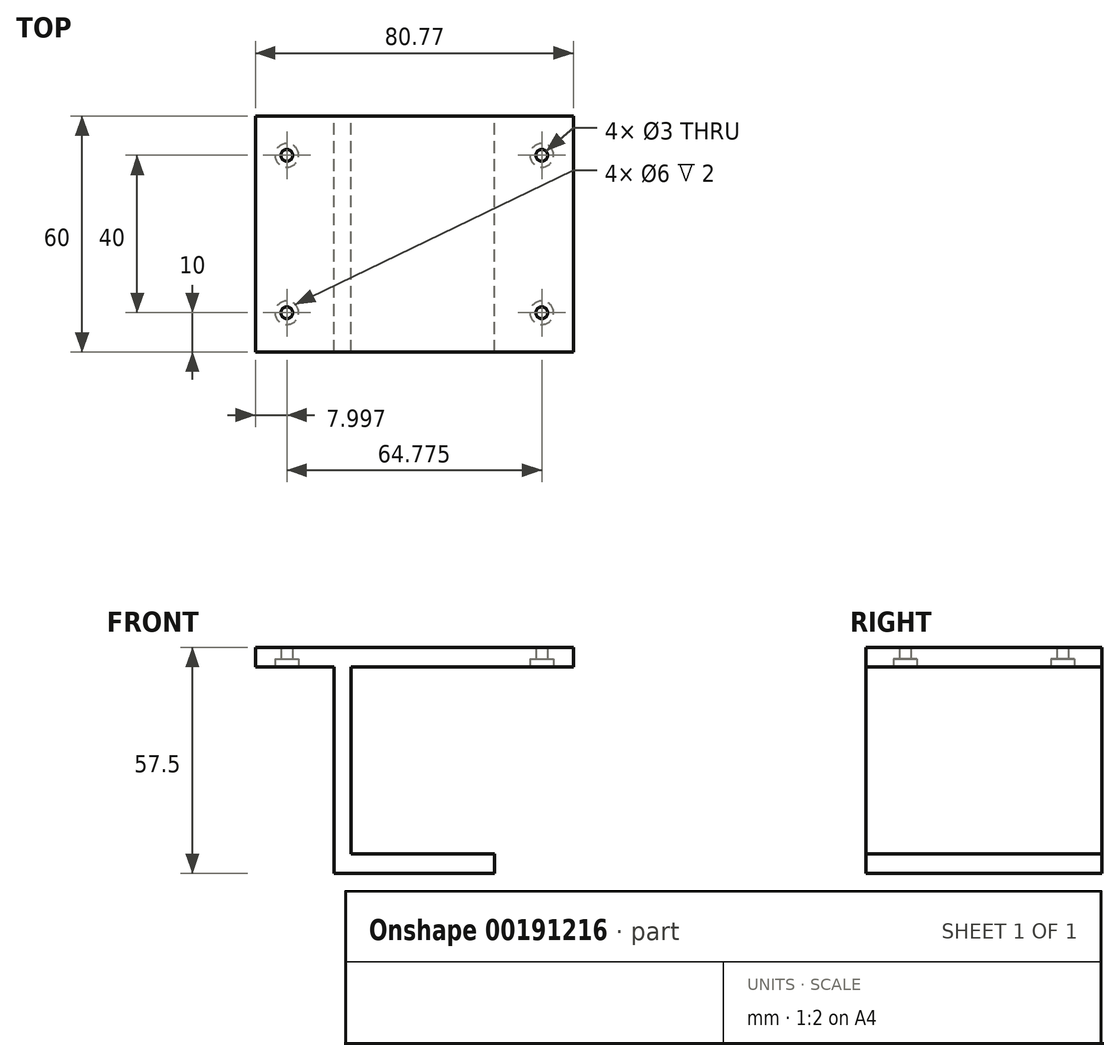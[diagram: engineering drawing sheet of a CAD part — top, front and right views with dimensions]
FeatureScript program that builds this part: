
annotation { "Feature Type Name" : "Feature", "Feature Type Description" : "" }
export const myFeature = defineFeature(function(context is Context, id is Id, definition is map)
    precondition{}
    {
        {
            var Q0;
            Q0=qCreatedBy(makeId("Front.planeOp"),FACE);
            var sketch = newSketch(context, id + "F0", { "sketchPlane" : qUnion([Q0])});
            skLineSegment(sketch, "E0.top", {"start": v(-27.45, -17.57) * mm, "end": v(13.32, -17.57) * mm});
            skLineSegment(sketch, "E0.left", {"start": v(-27.45, 34.93) * mm, "end": v(-27.45, -12.57) * mm});
            skLineSegment(sketch, "E1", {"start": v(13.32, -12.57) * mm, "end": v(-23.18, -12.57) * mm});
            skLineSegment(sketch, "E2", {"start": v(-23.18, -12.57) * mm, "end": v(-23.18, 34.93) * mm});
            skLineSegment(sketch, "E3", {"start": v(-23.18, 34.93) * mm, "end": v(13.32, 34.93) * mm});
            skLineSegment(sketch, "E4", {"start": v(13.32, 39.93) * mm, "end": v(-27.45, 39.93) * mm});
            skPoint(sketch, "E5.orphan", {"position": v(-27.45, 42.43) * mm});
            skLineSegment(sketch, "E6", {"start": v(13.32, 39.93) * mm, "end": v(33.32, 39.93) * mm});
            skLineSegment(sketch, "E7", {"start": v(33.32, 39.93) * mm, "end": v(33.32, 34.93) * mm});
            skLineSegment(sketch, "E8", {"start": v(33.32, 34.93) * mm, "end": v(13.32, 34.93) * mm});
            skLineSegment(sketch, "E9", {"start": v(13.32, -12.57) * mm, "end": v(13.32, -17.57) * mm});
            skLineSegment(sketch, "E10", {"start": v(-27.45, -12.57) * mm, "end": v(-27.45, -17.57) * mm});
            skPoint(sketch, "E11.end.orphan", {"position": v(-49.27, 34.93) * mm});
            skPoint(sketch, "E12.end.orphan", {"position": v(-49.27, -12.57) * mm});
            skLineSegment(sketch, "E13", {"start": v(-27.45, 39.93) * mm, "end": v(-47.45, 39.93) * mm});
            skLineSegment(sketch, "E14", {"start": v(-47.45, 39.93) * mm, "end": v(-47.45, 34.93) * mm});
            skLineSegment(sketch, "E15", {"start": v(-47.45, 34.93) * mm, "end": v(-27.45, 34.93) * mm});
            skSolve(sketch);
        }
        {
            var Q0;
            Q0=makeQuery(id+"F0.imprint","IMPRINT",FACE,{"disambiguationData":[TD([[makeQuery(id+"F0.imprint","IMPRINT",EDGE,{"derivedFrom":sQuery(id+"F0.wireOp",EDGE,"E0.top")}),1.0]])]});
            extrude(context, id + "F1", {"entities" : qUnion([Q0]), "depth" : 60 * mm});
        }
        {
            var Q0;
            Q0=makeQuery(id+"F1.opExtrude","SWEPT_FACE",FACE,{"disambiguationData":[OSD([sQuery(id+"F0.wireOp",EDGE,"E3"),sQuery(id+"F0.wireOp",EDGE,"E8")])]});
            var sketch = newSketch(context, id + "F2", { "sketchPlane" : qUnion([Q0])});
            skPoint(sketch, "E16", {"position": v(-39.45, 50) * mm});
            skPoint(sketch, "E17", {"position": v(-39.45, 10) * mm});
            skPoint(sketch, "E18", {"position": v(25.32, 50) * mm});
            skPoint(sketch, "E19", {"position": v(25.32, 10) * mm});
            skSolve(sketch);
        }
        {
            var Q0;
            Q0=sQuery(id+"F2.wireOp",VERTEX,"E18");
            var Q1;
            Q1=sQuery(id+"F2.wireOp",VERTEX,"E19");
            var Q2;
            Q2=sQuery(id+"F2.wireOp",VERTEX,"E17");
            var Q3;
            Q3=sQuery(id+"F2.wireOp",VERTEX,"E16");
            var Q4;
            Q4=makeQuery(id+"F1.opExtrude","SWEPT_BODY",BODY,{"disambiguationData":[OSD([sQuery(id+"F0.wireOp",EDGE,"E0.top"),sQuery(id+"F0.wireOp",EDGE,"E0.left"),sQuery(id+"F0.wireOp",EDGE,"E1"),sQuery(id+"F0.wireOp",EDGE,"E2"),sQuery(id+"F0.wireOp",EDGE,"E3"),sQuery(id+"F0.wireOp",EDGE,"E4"),sQuery(id+"F0.wireOp",EDGE,"E6"),sQuery(id+"F0.wireOp",EDGE,"E7"),sQuery(id+"F0.wireOp",EDGE,"E8"),sQuery(id+"F0.wireOp",EDGE,"E9"),sQuery(id+"F0.wireOp",EDGE,"E10"),sQuery(id+"F0.wireOp",EDGE,"E13"),sQuery(id+"F0.wireOp",EDGE,"E14"),sQuery(id+"F0.wireOp",EDGE,"E15")])]});
            hole(context, id + "F3", {"style" : HoleStyle.C_BORE, "endStyle" : HoleEndStyle.BLIND, "holeDiameter" : 3 * mm, "cBoreDiameter" : 6 * mm, "cBoreDepth" : 2 * mm, "holeDepth" : 8 * mm, "startFromSketch" : true, "locations" : qUnion([Q0, Q1, Q2, Q3]), "scope" : qUnion([Q4])});
        }
    });
